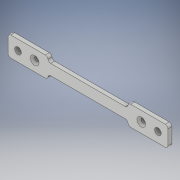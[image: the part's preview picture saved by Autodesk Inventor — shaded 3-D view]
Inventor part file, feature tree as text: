
AUTODESK INVENTOR PART (.ipt)
format: ipt  version: 2019 (Build 230136000, 136)  size: 152,576 bytes
history: native  units: mm
features: sketch x3, extrude x2, hole x1, plane x1, mirror x1, fillet x1
ambient origin geometry x8: Origin, YZ Plane, XZ Plane, XY Plane, X Axis, Y Axis, Z Axis, Center Point
bodies: Solid1 (feature_tree)
feature tree (9):
  extrude  "Extrusion1"  Depth=15.0mm
  hole  "Hole1"  [1 undecoded]
  extrude  "Extrusion2"  Depth=3.0mm TaperAngle=0.0deg
  plane  "Work Plane1"
  mirror  "Mirror1"
  fillet  "Fillet1"  Radius=80.0mm
  sketch  "Sketch1"  dims[d0=120.0mm d1=15.0mm]
  sketch  "Sketch2"  dims[d2=5.0mm d3=7.5mm]
  sketch  "Sketch3"  dims[d4=7.5mm d5=3.0mm d6=0.0mm d7=80.0mm d8=3.3mm d9=6.0mm d10=6.5mm d11=2.0mm d12=90.0deg d13=36.25mm d14=0.0mm d15=2.0mm d16=10.0mm d17=10.0mm d18=4.0mm d19=3.0mm d20=0.0mm]
note: 1 required parameter value undecoded (feature->parameter linkage not recoverable at this tier; creation-order binding heuristic only, values carry confidence <= 0.55)
